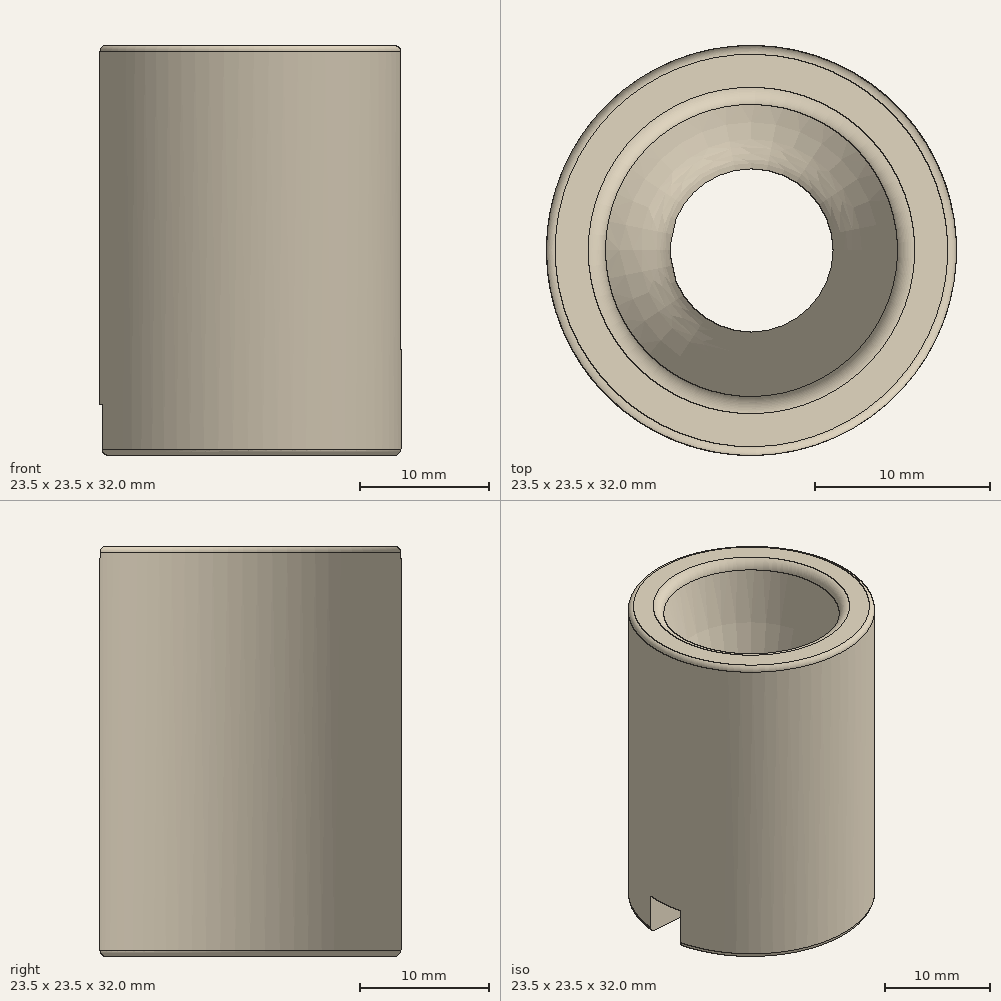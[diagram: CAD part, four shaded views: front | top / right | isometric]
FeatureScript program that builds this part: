
annotation { "Feature Type Name" : "Feature", "Feature Type Description" : "" }
export const myFeature = defineFeature(function(context is Context, id is Id, definition is map)
    precondition{}
    {
        {
            var Q0;
            Q0=qCreatedBy(makeId("Front.planeOp"),FACE);
            var sketch = newSketch(context, id + "F0", { "sketchPlane" : qUnion([Q0])});
            skLineSegment(sketch, "E0", {"start": v(0, 0) * mm, "end": v(4.95, 0) * mm, "construction": true});
            skLineSegment(sketch, "E1", {"start": v(0, 0) * mm, "end": v(0, 13) * mm, "construction": true});
            skLineSegment(sketch, "E2", {"start": v(0, 13) * mm, "end": v(8.5, 13) * mm, "construction": true});
            skLineSegment(sketch, "E3", {"start": v(8.5, 13) * mm, "end": v(11.75, 13) * mm});
            skLineSegment(sketch, "E4", {"start": v(4.95, -12) * mm, "end": v(5.45, -12) * mm});
            skLineSegment(sketch, "E5", {"start": v(5.45, -12) * mm, "end": v(5.45, -19) * mm});
            skLineSegment(sketch, "E6", {"start": v(5.45, -19) * mm, "end": v(11.75, -19) * mm});
            skLineSegment(sketch, "E7", {"start": v(11.75, -19) * mm, "end": v(11.75, 13) * mm});
            skFitSpline(sketch, "E8", {"points": [v(4.95, -12) * mm, v(4.95, 0) * mm, v(8.5, 13) * mm], "startDerivative": vector(-1.25, 27.83) * mm, "endDerivative": vector(8.57, 56.77) * mm});
            skSolve(sketch);
        }
        {
            var Q0;
            Q0 = qSketchRegion(id + "F0", true);
            var Q1;
            Q1=sQuery(id+"F0.wireOp",EDGE,"E1");
            revolve(context, id + "F1", {"surfaceOperationType" : NewSurfaceOperationType.NEW, "entities" : qUnion([Q0]), "axis" : qUnion([Q1]), "revolveType" : RevolveType.FULL});
        }
        {
            var Q0;
            Q0=makeQuery(id+"F1.opRevolve","SWEPT_EDGE",EDGE,{"disambiguationData":[OSD([sQuery(id+"F0.wireOp",EDGE,"E3"),sQuery(id+"F0.wireOp",EDGE,"E7")])]});
            var Q1;
            Q1=makeQuery(id+"F1.opRevolve","SWEPT_EDGE",EDGE,{"disambiguationData":[OSD([sQuery(id+"F0.wireOp",EDGE,"E6"),sQuery(id+"F0.wireOp",EDGE,"E7")])]});
            var Q2;
            Q2=makeQuery(id+"F1.opRevolve","SWEPT_EDGE",EDGE,{"disambiguationData":[OSD([sQuery(id+"F0.wireOp",EDGE,"E5"),sQuery(id+"F0.wireOp",EDGE,"E6")])]});
            fillet(context, id + "F2", {"entities" : qUnion([Q0, Q1, Q2]), "radius" : .5 * mm, "tangentPropagation" : true, "allowEdgeOverflow" : false});
        }
        {
            var Q0;
            Q0=makeQuery(id+"F1.opRevolve","SWEPT_EDGE",EDGE,{"disambiguationData":[OSD([sQuery(id+"F0.wireOp",EDGE,"E3"),sQuery(id+"F0.wireOp",EDGE,"E8")])]});
            fillet(context, id + "F3", {"entities" : qUnion([Q0]), "radius" : 1 * mm, "tangentPropagation" : true, "allowEdgeOverflow" : false});
        }
        {
            var Q0;
            Q0=makeQuery(id+"F1.opRevolve","SWEPT_FACE",FACE,{"disambiguationData":[OSD([sQuery(id+"F0.wireOp",EDGE,"E6")])]});
            var sketch = newSketch(context, id + "F4", { "sketchPlane" : qUnion([Q0])});
            skLineSegment(sketch, "E9", {"start": v(-5.95, 0) * mm, "end": v(-8.7, 0) * mm, "construction": true});
            skLineSegment(sketch, "E10.bottom", {"start": v(-12.7, 2) * mm, "end": v(-4.7, 2) * mm});
            skLineSegment(sketch, "E10.top", {"start": v(-12.7, -2) * mm, "end": v(-4.7, -2) * mm});
            skLineSegment(sketch, "E10.left", {"start": v(-12.7, 2) * mm, "end": v(-12.7, -2) * mm});
            skLineSegment(sketch, "E10.right", {"start": v(-4.7, 2) * mm, "end": v(-4.7, -2) * mm});
            skPoint(sketch, "E10.middle", {"position": v(-8.7, 0) * mm});
            skSolve(sketch);
        }
        {
            var Q0;
            Q0 = qSketchRegion(id + "F4", true);
            extrude(context, id + "F5", {"entities" : qUnion([Q0]), "operationType" : NewBodyOperationType.REMOVE, "oppositeDirection" : true, "depth" : 4 * mm, "offsetDistance" : 25 * mm});
        }
    });
